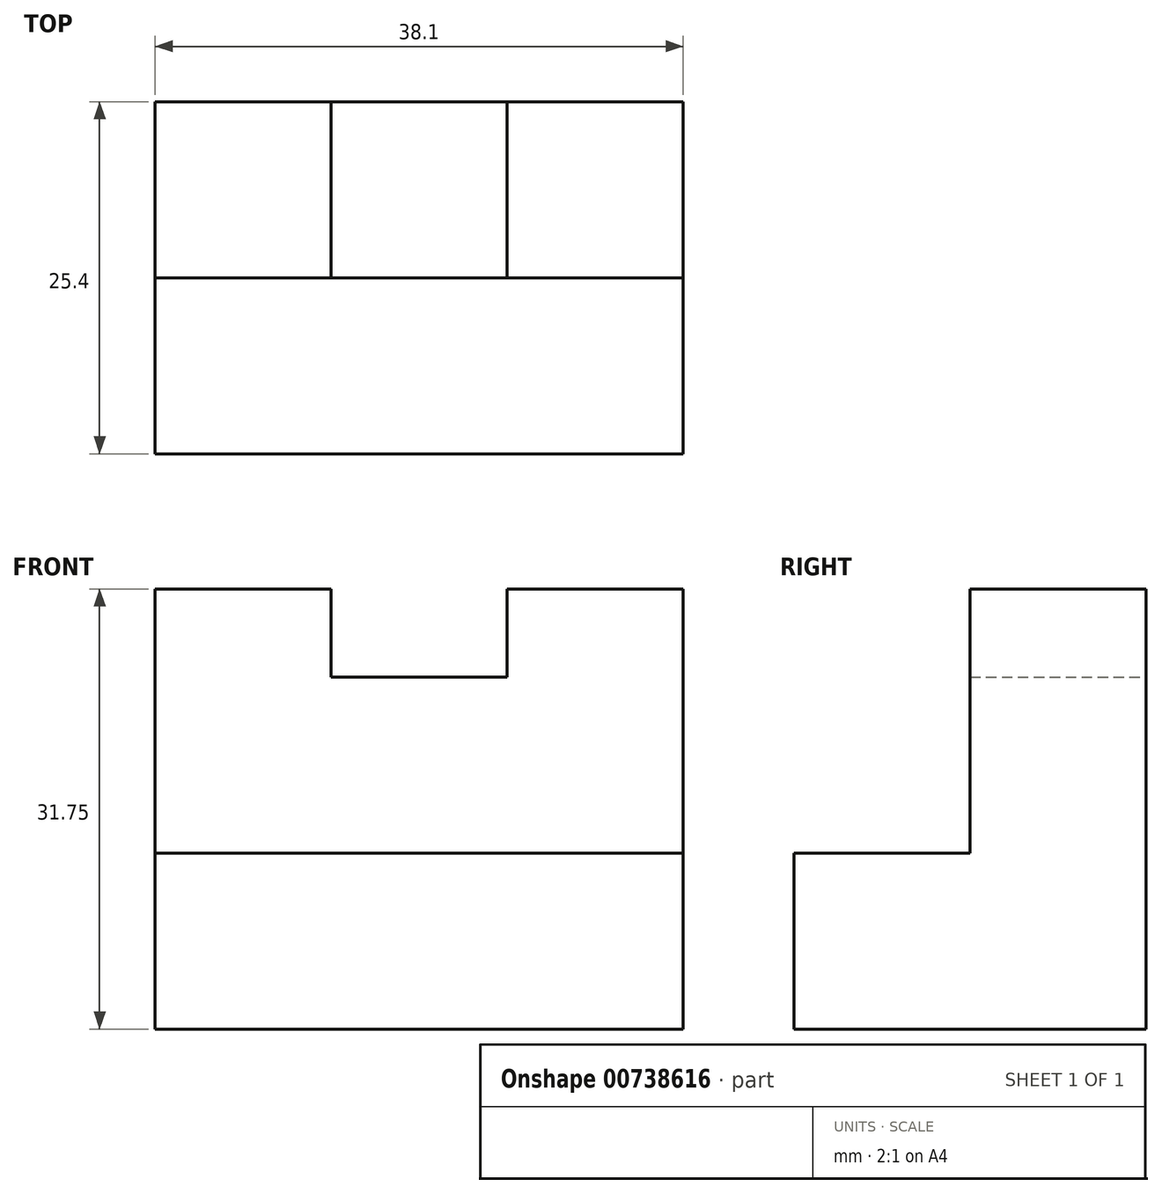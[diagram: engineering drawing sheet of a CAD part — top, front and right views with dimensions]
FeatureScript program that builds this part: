
annotation { "Feature Type Name" : "Feature", "Feature Type Description" : "" }
export const myFeature = defineFeature(function(context is Context, id is Id, definition is map)
    precondition{}
    {
        {
            var Q0;
            Q0=qCreatedBy(makeId("Top.planeOp"),FACE);
            var sketch = newSketch(context, id + "F0", { "sketchPlane" : qUnion([Q0])});
            skLineSegment(sketch, "E0.bottom", {"start": v(38.1, 36.92) * mm, "end": v(0, 36.92) * mm});
            skLineSegment(sketch, "E0.top", {"start": v(38.1, 11.52) * mm, "end": v(0, 11.52) * mm});
            skLineSegment(sketch, "E0.left", {"start": v(38.1, 36.92) * mm, "end": v(38.1, 11.52) * mm});
            skLineSegment(sketch, "E0.right", {"start": v(0, 36.92) * mm, "end": v(0, 11.52) * mm});
            skSolve(sketch);
        }
        {
            var Q0;
            Q0 = qSketchRegion(id + "F0", true);
            extrude(context, id + "F1", {"entities" : qUnion([Q0]), "depth" : 31.75 * mm, "offsetDistance" : 25.4 * mm});
        }
        {
            var Q0;
            Q0=makeQuery(id+"F1.opExtrude","CAP_FACE",FACE,{"disambiguationData":[OSD([sQuery(id+"F0.wireOp",EDGE,"E0.bottom"),sQuery(id+"F0.wireOp",EDGE,"E0.top"),sQuery(id+"F0.wireOp",EDGE,"E0.left"),sQuery(id+"F0.wireOp",EDGE,"E0.right")])],"isStart":false});
            var sketch = newSketch(context, id + "F2", { "sketchPlane" : qUnion([Q0])});
            skLineSegment(sketch, "E1.bottom", {"start": v(38.1, 24.22) * mm, "end": v(0, 24.22) * mm});
            skLineSegment(sketch, "E1.top", {"start": v(38.1, 11.52) * mm, "end": v(0, 11.52) * mm});
            skLineSegment(sketch, "E1.left", {"start": v(38.1, 24.22) * mm, "end": v(38.1, 11.52) * mm});
            skLineSegment(sketch, "E1.right", {"start": v(0, 24.22) * mm, "end": v(0, 11.52) * mm});
            skSolve(sketch);
        }
        {
            var Q0;
            Q0=makeQuery(id+"F2.imprint","IMPRINT",FACE,{"disambiguationData":[TD([[makeQuery(id+"F2.imprint","IMPRINT",EDGE,{"derivedFrom":sQuery(id+"F2.wireOp",EDGE,"E1.bottom")}),1.0]])]});
            extrude(context, id + "F3", {"entities" : qUnion([Q0]), "operationType" : NewBodyOperationType.REMOVE, "oppositeDirection" : true, "depth" : 19.05 * mm, "offsetDistance" : 25.4 * mm});
        }
        {
            var Q0;
            Q0=makeQuery(id+"F1.opExtrude","CAP_FACE",FACE,{"disambiguationData":[OSD([sQuery(id+"F0.wireOp",EDGE,"E0.bottom"),sQuery(id+"F0.wireOp",EDGE,"E0.top"),sQuery(id+"F0.wireOp",EDGE,"E0.left"),sQuery(id+"F0.wireOp",EDGE,"E0.right")])],"isStart":false});
            var sketch = newSketch(context, id + "F4", { "sketchPlane" : qUnion([Q0])});
            skLineSegment(sketch, "E2", {"start": v(0, 24.22) * mm, "end": v(12.7, 24.22) * mm});
            skLineSegment(sketch, "E3.bottom", {"start": v(12.7, 24.22) * mm, "end": v(25.4, 24.22) * mm});
            skLineSegment(sketch, "E3.top", {"start": v(12.7, 36.92) * mm, "end": v(25.4, 36.92) * mm});
            skLineSegment(sketch, "E3.left", {"start": v(12.7, 24.22) * mm, "end": v(12.7, 36.92) * mm});
            skLineSegment(sketch, "E3.right", {"start": v(25.4, 24.22) * mm, "end": v(25.4, 36.92) * mm});
            skSolve(sketch);
        }
        {
            var Q0;
            Q0=makeQuery(id+"F4.imprint","IMPRINT",FACE,{"disambiguationData":[TD([[makeQuery(id+"F4.imprint","IMPRINT",EDGE,{"derivedFrom":sQuery(id+"F4.wireOp",EDGE,"E3.bottom")}),-1.0]])]});
            extrude(context, id + "F5", {"entities" : qUnion([Q0]), "operationType" : NewBodyOperationType.REMOVE, "oppositeDirection" : true, "depth" : 6.35 * mm, "offsetDistance" : 25.4 * mm});
        }
    });
